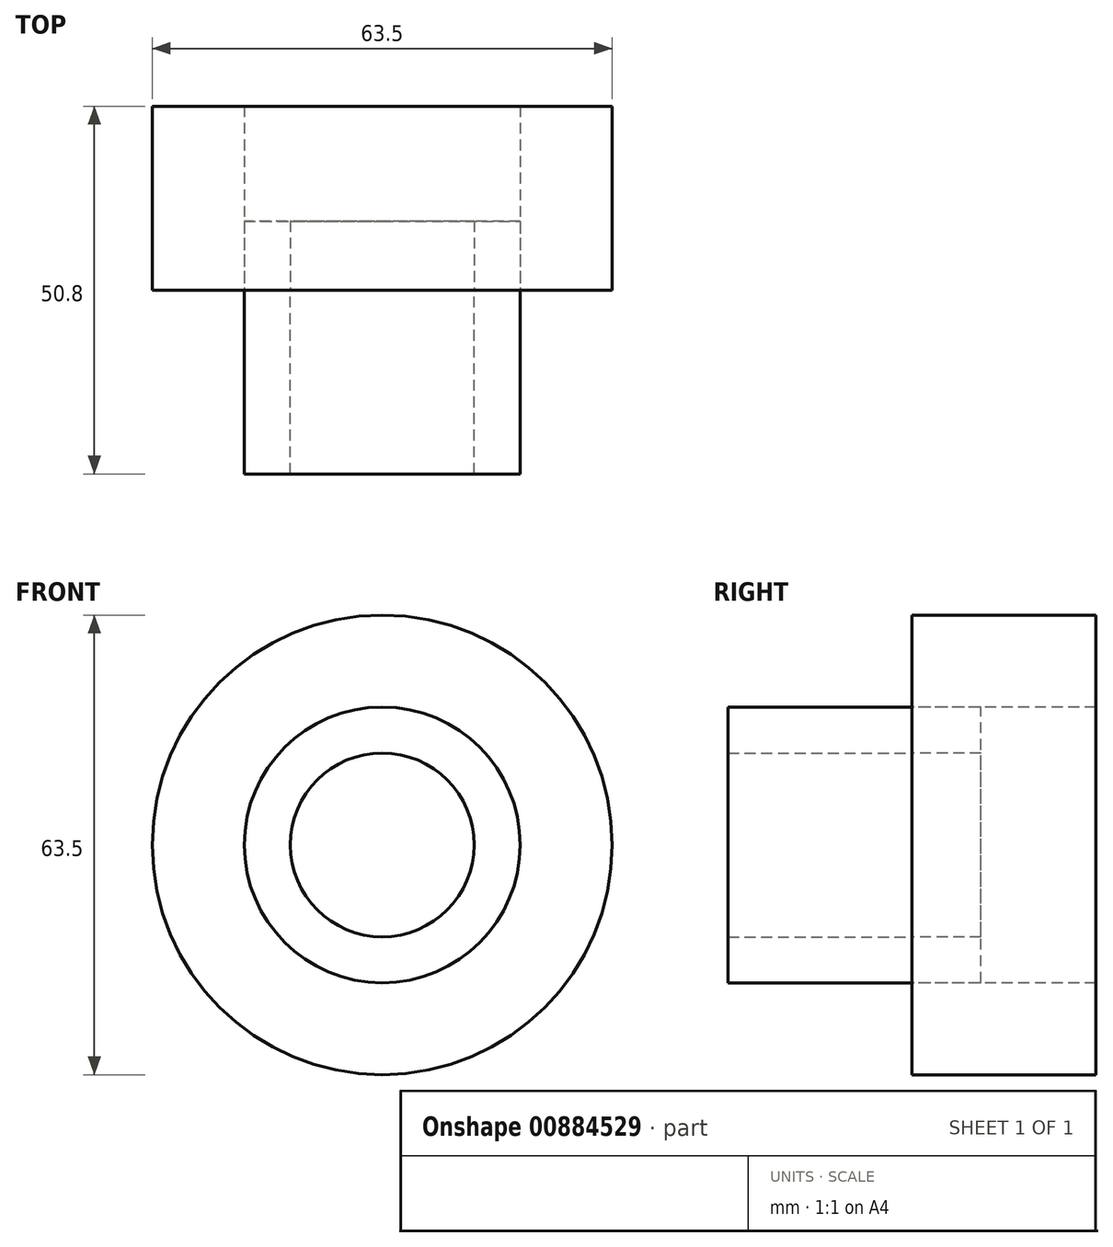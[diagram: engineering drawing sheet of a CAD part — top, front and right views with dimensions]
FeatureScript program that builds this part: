
annotation { "Feature Type Name" : "Feature", "Feature Type Description" : "" }
export const myFeature = defineFeature(function(context is Context, id is Id, definition is map)
    precondition{}
    {
        {
            var Q0;
            Q0=qCreatedBy(makeId("Front.planeOp"),FACE);
            var sketch = newSketch(context, id + "F0", { "sketchPlane" : qUnion([Q0])});
            skCircle(sketch, "E0", {"center": v(0, 0) * mm, "radius": 31.75 * mm});
            skCircle(sketch, "E1", {"center": v(0, 0) * mm, "radius": 12.7 * mm});
            skCircle(sketch, "E2", {"center": v(0, 0) * mm, "radius": 19.05 * mm});
            skSolve(sketch);
        }
        {
            var Q0;
            Q0=makeQuery(id+"F0.imprint","IMPRINT",FACE,{"disambiguationData":[TD([[makeQuery(id+"F0.imprint","IMPRINT",EDGE,{"derivedFrom":sQuery(id+"F0.wireOp",EDGE,"E1")}),-1.0]])]});
            extrude(context, id + "F1", {"entities" : qUnion([Q0]), "depth" : 25.4 * mm, "offsetDistance" : 25.4 * mm});
        }
        {
            var Q0;
            Q0 = qSketchRegion(id + "F0", true);
            extrude(context, id + "F2", {"entities" : qUnion([Q0]), "operationType" : NewBodyOperationType.ADD, "oppositeDirection" : true, "depth" : 25.4 * mm, "offsetDistance" : 25.4 * mm});
        }
        {
            var Q0;
            Q0=makeQuery(id+"F1.opExtrude","CAP_FACE",FACE,{"disambiguationData":[OSD([sQuery(id+"F0.wireOp",EDGE,"E1"),sQuery(id+"F0.wireOp",EDGE,"E2")])],"isStart":true});
            extrude(context, id + "F3", {"entities" : qUnion([Q0]), "depth" : 9.52 * mm, "offsetDistance" : 25.4 * mm});
        }
    });
